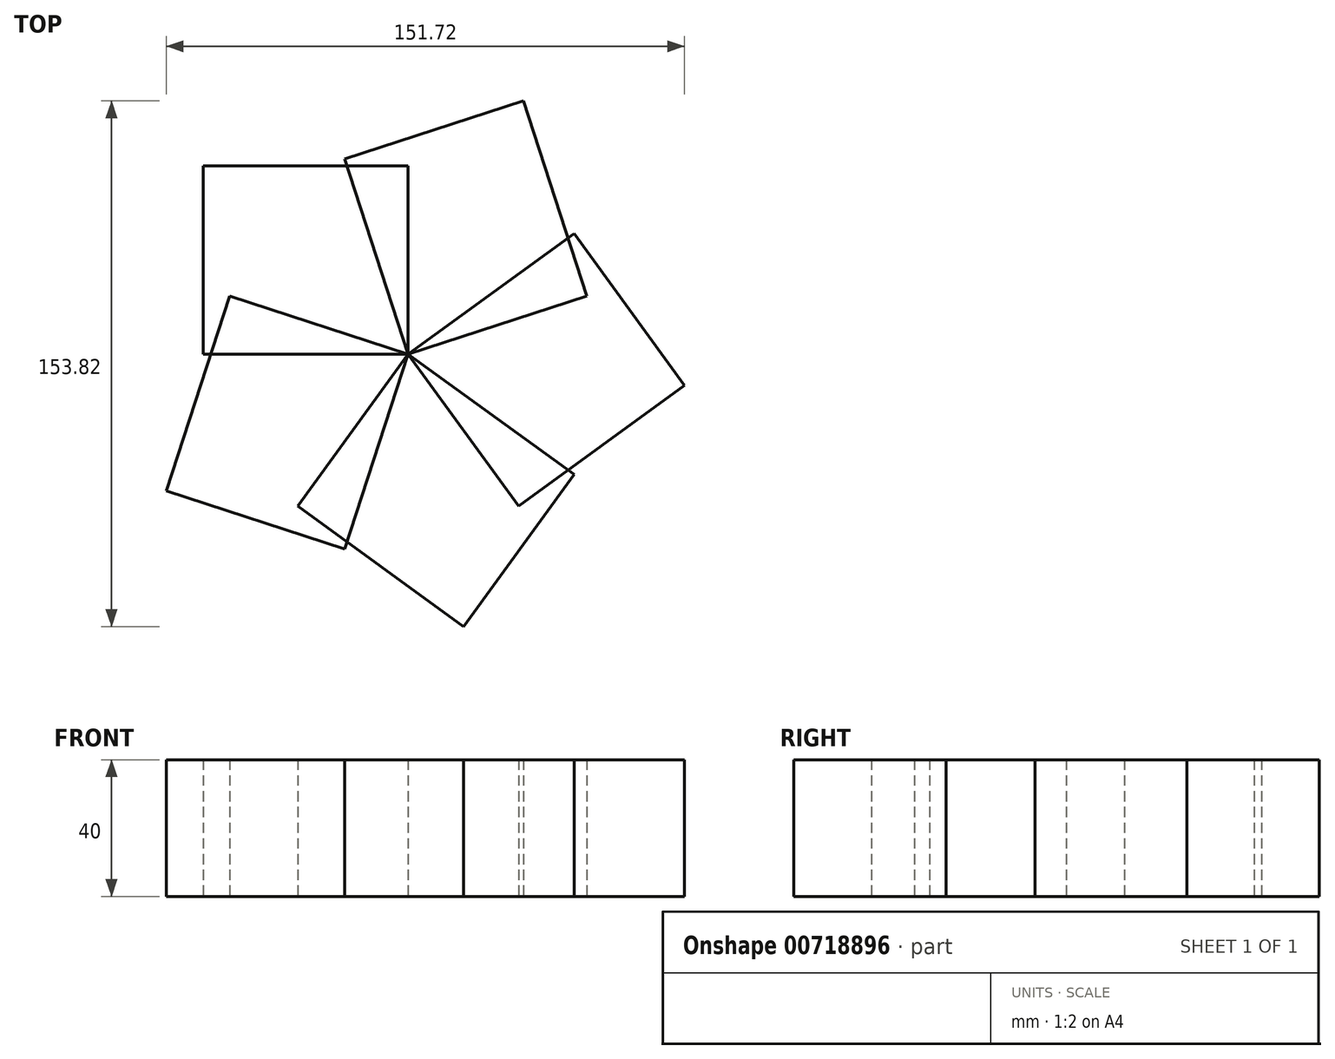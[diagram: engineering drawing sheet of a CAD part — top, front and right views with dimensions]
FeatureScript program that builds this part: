
annotation { "Feature Type Name" : "Feature", "Feature Type Description" : "" }
export const myFeature = defineFeature(function(context is Context, id is Id, definition is map)
    precondition{}
    {
        {
            var Q0;
            Q0=qCreatedBy(makeId("Top.planeOp"),FACE);
            var sketch = newSketch(context, id + "F0", { "sketchPlane" : qUnion([Q0])});
            skLineSegment(sketch, "E0.bottom", {"start": v(0, 0) * mm, "end": v(-60, 0) * mm});
            skLineSegment(sketch, "E0.top", {"start": v(0, 55) * mm, "end": v(-60, 55) * mm});
            skLineSegment(sketch, "E0.left", {"start": v(0, 0) * mm, "end": v(0, 55) * mm});
            skLineSegment(sketch, "E0.right", {"start": v(-60, 0) * mm, "end": v(-60, 55) * mm});
            skSolve(sketch);
        }
        {
            var Q0;
            Q0=makeQuery(id+"F0.imprint","IMPRINT",FACE,{"disambiguationData":[TD([[makeQuery(id+"F0.imprint","IMPRINT",EDGE,{"derivedFrom":sQuery(id+"F0.wireOp",EDGE,"E0.bottom")}),-1.0]])]});
            extrude(context, id + "F1", {"entities" : qUnion([Q0]), "depth" : 40 * mm, "offsetDistance" : 25 * mm});
        }
        {
            var Q0;
            Q0=makeQuery(id+"F1.opExtrude","SWEPT_BODY",BODY,{"disambiguationData":[OSD([sQuery(id+"F0.wireOp",EDGE,"E0.bottom"),sQuery(id+"F0.wireOp",EDGE,"E0.top"),sQuery(id+"F0.wireOp",EDGE,"E0.left"),sQuery(id+"F0.wireOp",EDGE,"E0.right")])]});
            var Q1;
            Q1=makeQuery(id+"F1.opExtrude","SWEPT_EDGE",EDGE,{"disambiguationData":[OSD([sQuery(id+"F0.wireOp",EDGE,"E0.bottom"),sQuery(id+"F0.wireOp",EDGE,"E0.left")])]});
            circularPattern(context, id + "F2", {"entities" : qUnion([Q0]), "axis" : qUnion([Q1]), "angle" : 360 * degree, "instanceCount" : 5, "equalSpace" : true});
        }
    });
